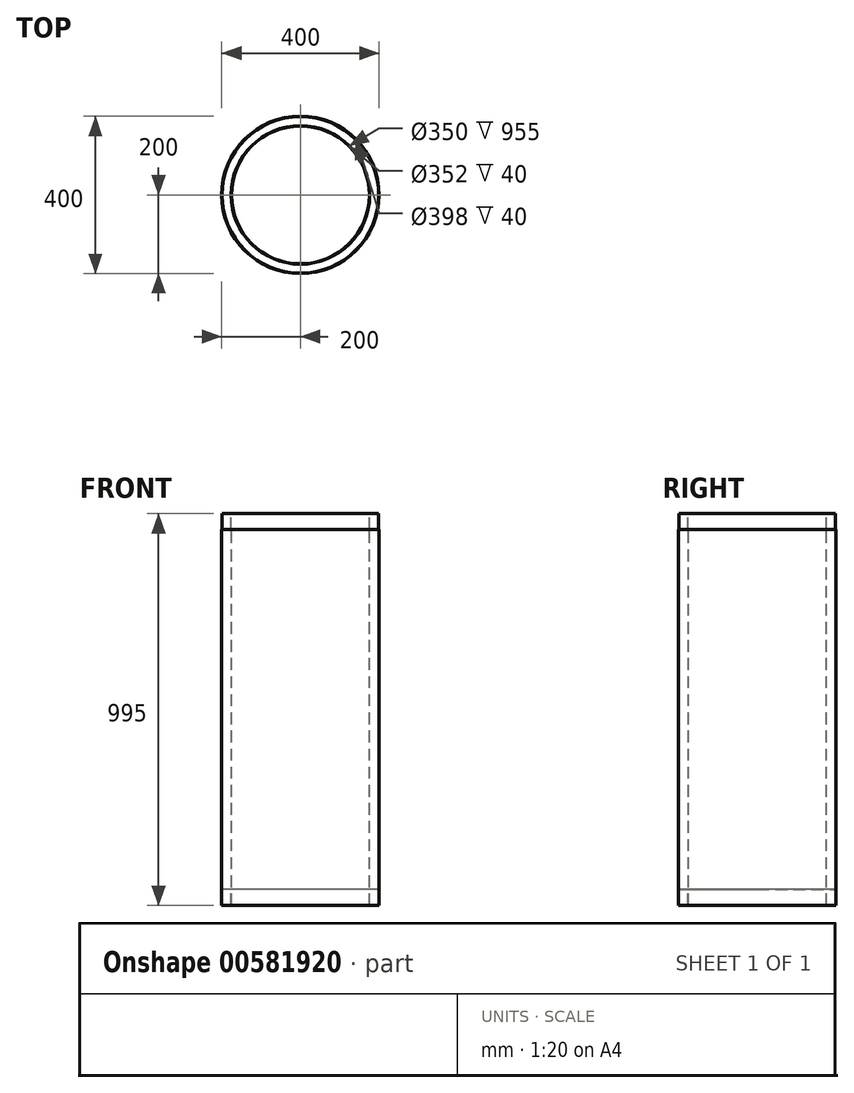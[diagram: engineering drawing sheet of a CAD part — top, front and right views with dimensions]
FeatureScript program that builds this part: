
annotation { "Feature Type Name" : "Feature", "Feature Type Description" : "" }
export const myFeature = defineFeature(function(context is Context, id is Id, definition is map)
    precondition{}
    {
        {
            var Q0;
            Q0=qCreatedBy(makeId("Front.planeOp"),FACE);
            var sketch = newSketch(context, id + "F0", { "sketchPlane" : qUnion([Q0])});
            skLineSegment(sketch, "E0", {"start": v(0, 345.75) * mm, "end": v(0, -558.03) * mm, "construction": true});
            skLineSegment(sketch, "E1", {"start": v(-175, -518.84) * mm, "end": v(-175, 436.16) * mm});
            skLineSegment(sketch, "E2", {"start": v(-175, 436.16) * mm, "end": v(-176, 436.16) * mm});
            skLineSegment(sketch, "E3", {"start": v(-176, 436.16) * mm, "end": v(-176, 476.16) * mm});
            skLineSegment(sketch, "E4", {"start": v(-176, 476.16) * mm, "end": v(-199, 476.16) * mm});
            skLineSegment(sketch, "E5", {"start": v(-199, 476.16) * mm, "end": v(-199, 436.16) * mm});
            skLineSegment(sketch, "E6", {"start": v(-199, 436.16) * mm, "end": v(-200, 436.16) * mm});
            skLineSegment(sketch, "E7", {"start": v(-200, 436.16) * mm, "end": v(-200, -518.84) * mm});
            skLineSegment(sketch, "E8", {"start": v(-200, -518.84) * mm, "end": v(-199, -518.84) * mm});
            skLineSegment(sketch, "E9", {"start": v(-199, -518.84) * mm, "end": v(-199, -478.84) * mm});
            skLineSegment(sketch, "E10", {"start": v(-199, -478.84) * mm, "end": v(-176, -478.84) * mm});
            skLineSegment(sketch, "E11", {"start": v(-176, -478.84) * mm, "end": v(-176, -518.84) * mm});
            skLineSegment(sketch, "E12", {"start": v(-176, -518.84) * mm, "end": v(-175, -518.84) * mm});
            skSolve(sketch);
        }
        {
            var Q0;
            Q0=qSketchRegion(id+"F0",true);
            var Q1;
            Q1=sQuery(id+"F0.wireOp",EDGE,"E0");
            revolve(context, id + "F1", {"entities" : qUnion([Q0]), "axis" : qUnion([Q1]), "revolveType" : RevolveType.FULL});
        }
    });
